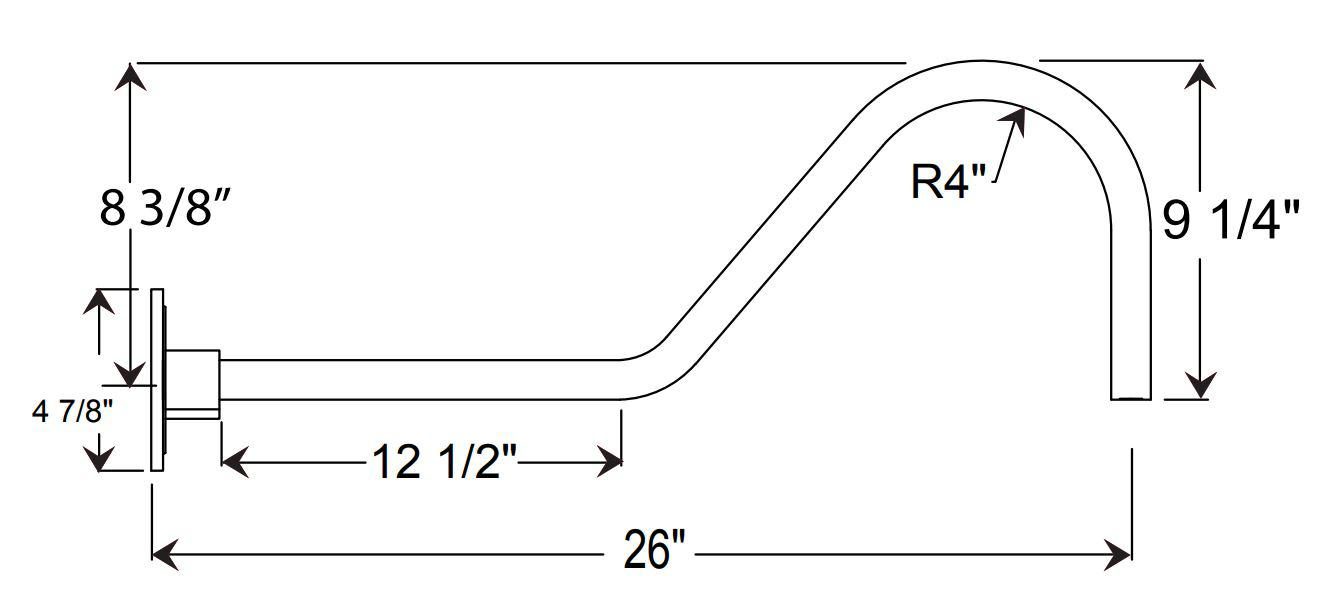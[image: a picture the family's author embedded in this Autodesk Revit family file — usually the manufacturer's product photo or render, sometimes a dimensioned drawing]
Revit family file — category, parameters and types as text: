
# Revit family: OSPB LED 12,20,24
name_source: partatom
category: Lighting Fixtures
units: mm (PartAtom-declared; Revit-internal decimal feet)

## family parameters
Always vertical = Yes
Cut with Voids When Loaded = No
Light Source = Yes
OmniClass Number = 23.80.70.00
OmniClass Title = Lighting
Part Type = Normal
Room Calculation Point = No
Round Connector Dimension = Use Diameter
Shared = No
Work Plane-Based = No

## types (3) — shared parameters
Apparent Load = 37 VA
Body Colour = Spun aluminium
Body Material = body
CRI = >90
Canopy Body = body
Color Filter = 16777215
Construction Material = Heavy Duty spun aluminum.
Default Elevation = 0' - 0"
Description = 120-277 Voltage
Dimming = 1%
Dimming Lamp Color Temperature Shift = <None>
Efficiency = 65-125 lumens per watt
GLASS = Bulb
INSIDE BODY = body
Lamp = LED
Life = L70 50,000 hours
Load Classification = Lighting
Manufacturer = ANP Lighting
Photometric Web File = generic
Power Factor = 1
Tilt Angle = 90.00°
URL = https://www.anplighting.com
Voltage = 277 V
Warranty = 5 year limited warranty
Wattage Comments = 37 W

## per-type parameters (varying)
| type | Fixture Diameter | Fixture Height | OSPB12 | OSPB20 | OSPB24 | Weight | a | b |
| OSPB12 | 1' - 0" | 2' - 0" | Yes | No | No | 13.5 lbs | 2' - 0" | 0' - 3" |
| OSPB20 | 1' - 8" | 3' - 0" | No | Yes | No | 22.0 lbs | 3' - 0" | 0' - 5" |
| OSPB24 | 2' - 0" | 3' - 6" | No | No | Yes | 28.5 lbs | 3' - 6" | 1' - 2" |

note: column(s) folded — value = type name in every type: Model

## geometry (parser evidence)
native form markers: Sweep x28
no freeform markers — native parametric forms only
